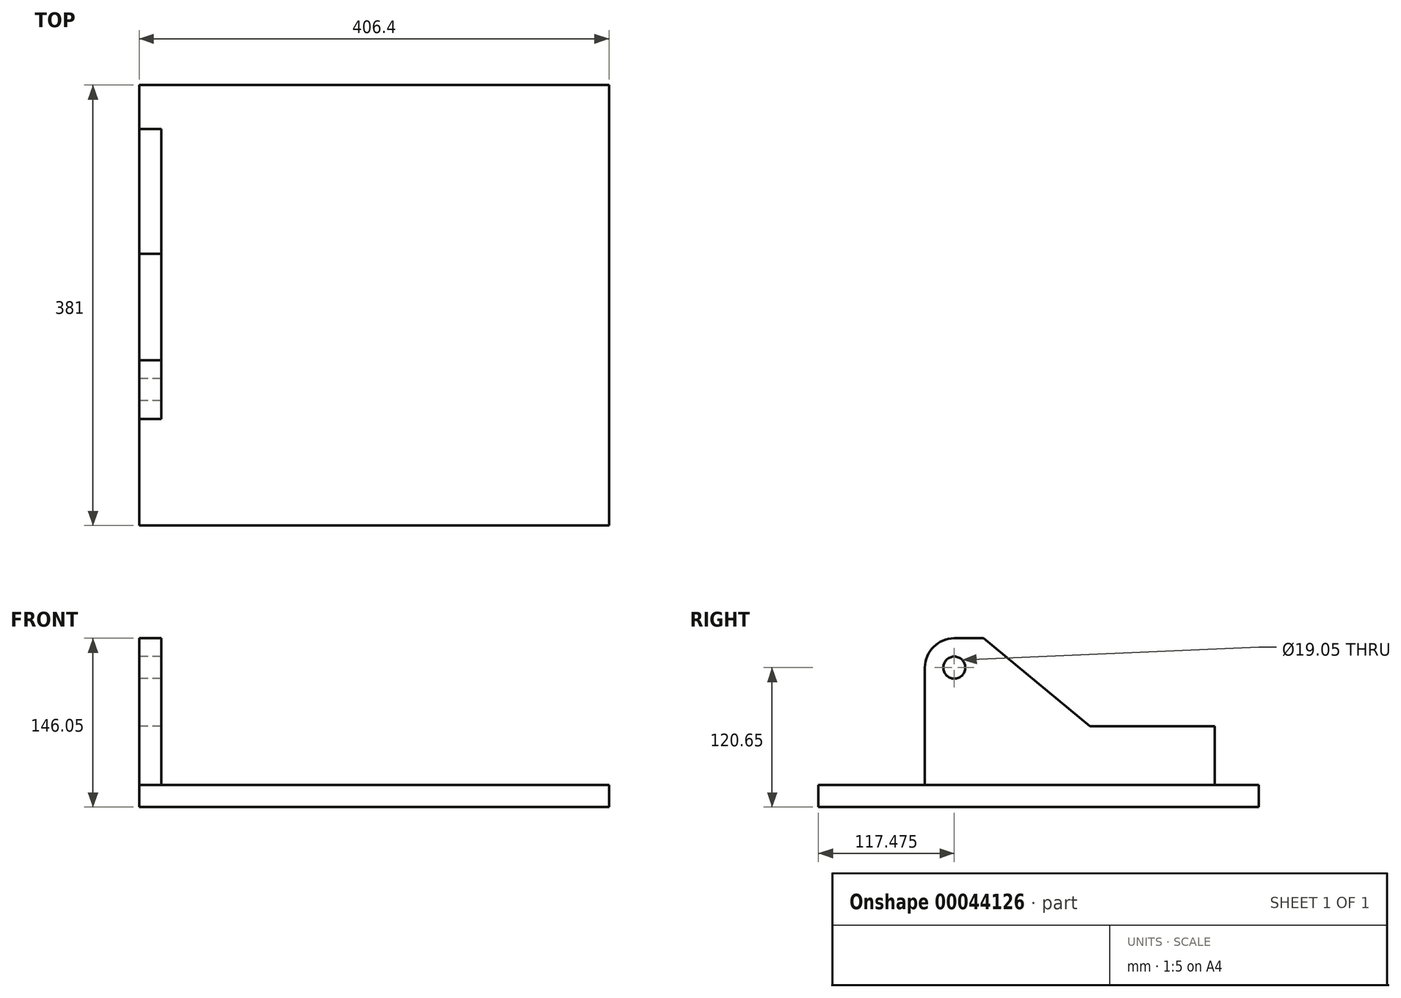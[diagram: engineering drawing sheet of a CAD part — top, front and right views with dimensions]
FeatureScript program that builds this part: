
annotation { "Feature Type Name" : "Feature", "Feature Type Description" : "" }
export const myFeature = defineFeature(function(context is Context, id is Id, definition is map)
    precondition{}
    {
        {
            var Q0;
            Q0=qCreatedBy(makeId("Right.planeOp"),FACE);
            var sketch = newSketch(context, id + "F0", { "sketchPlane" : qUnion([Q0])});
            skLineSegment(sketch, "E0.bottom", {"start": v(0, 0) * mm, "end": v(381, 0) * mm, "construction": true});
            skLineSegment(sketch, "E0.top", {"start": v(92.08, 19.05) * mm, "end": v(381, 19.05) * mm, "construction": true});
            skLineSegment(sketch, "E0.right", {"start": v(381, 0) * mm, "end": v(381, 19.05) * mm, "construction": true});
            skLineSegment(sketch, "E1.top", {"start": v(381, 107.95) * mm, "end": v(342.9, 107.95) * mm, "construction": true});
            skLineSegment(sketch, "E1.left", {"start": v(381, 19.05) * mm, "end": v(381, 107.95) * mm, "construction": true});
            skLineSegment(sketch, "E1.right", {"start": v(342.9, 19.05) * mm, "end": v(342.9, 107.95) * mm, "construction": true});
            skLineSegment(sketch, "E2.bottom", {"start": v(92.08, 19.05) * mm, "end": v(142.88, 19.05) * mm, "construction": true});
            skLineSegment(sketch, "E2.top", {"start": v(117.48, 146.05) * mm, "end": v(142.88, 146.05) * mm, "construction": true});
            skLineSegment(sketch, "E2.left", {"start": v(92.08, 19.05) * mm, "end": v(92.08, 120.65) * mm, "construction": true});
            skLineSegment(sketch, "E2.right", {"start": v(142.88, 19.05) * mm, "end": v(142.88, 146.05) * mm, "construction": true});
            skCircle(sketch, "E3", {"center": v(117.48, 120.65) * mm, "radius": 9.53 * mm, "construction": true});
            skPoint(sketch, "E3.centerSnap0", {"position": v(117.48, 146.05) * mm});
            skPoint(sketch, "E4.visualSharp", {"position": v(92.08, 146.05) * mm});
            skArc(sketch, "E4.filletArc", {"start": v(117.48, 146.05) * mm, "mid": v(99.51, 138.61) * mm, "end": v(92.08, 120.65) * mm, "construction": true});
            skLineSegment(sketch, "E5", {"start": v(142.88, 146.05) * mm, "end": v(342.9, 107.95) * mm, "construction": true});
            skLineSegment(sketch, "E6", {"start": v(0, 0) * mm, "end": v(0, 19.05) * mm, "construction": true});
            skLineSegment(sketch, "E7", {"start": v(0, 19.05) * mm, "end": v(92.08, 19.05) * mm, "construction": true});
            skSolve(sketch);
        }
        {
            var Q0;
            Q0=qCreatedBy(makeId("Right.planeOp"),FACE);
            var sketch = newSketch(context, id + "F1", { "sketchPlane" : qUnion([Q0])});
            skLineSegment(sketch, "E8.bottom", {"start": v(0, 19.05) * mm, "end": v(381, 19.05) * mm});
            skLineSegment(sketch, "E8.top", {"start": v(0, 0) * mm, "end": v(381, 0) * mm});
            skLineSegment(sketch, "E8.left", {"start": v(0, 19.05) * mm, "end": v(0, 0) * mm});
            skLineSegment(sketch, "E8.right", {"start": v(381, 19.05) * mm, "end": v(381, 0) * mm});
            skLineSegment(sketch, "E9.bottom", {"start": v(381, 19.05) * mm, "end": v(342.9, 19.05) * mm});
            skLineSegment(sketch, "E9.top", {"start": v(381, 107.95) * mm, "end": v(342.9, 107.95) * mm});
            skLineSegment(sketch, "E9.left", {"start": v(381, 19.05) * mm, "end": v(381, 107.95) * mm});
            skLineSegment(sketch, "E9.right", {"start": v(342.9, 19.05) * mm, "end": v(342.9, 107.95) * mm});
            skSolve(sketch);
        }
        {
            var Q0;
            Q0=makeQuery(id+"F1.imprint","IMPRINT",FACE,{"disambiguationData":[TD([[makeQuery(id+"F1.imprint","IMPRINT",EDGE,{"derivedFrom":sQuery(id+"F1.wireOp",EDGE,"E8.bottom")}),-1.0]])]});
            var Q1;
            Q1=makeQuery(id+"F1.imprint","IMPRINT",FACE,{"disambiguationData":[TD([[makeQuery(id+"F1.imprint","IMPRINT",EDGE,{"derivedFrom":sQuery(id+"F1.wireOp",EDGE,"E9.bottom")}),-1.0]])]});
            extrude(context, id + "F2", {"entities" : qUnion([Q0, Q1]), "depth" : 406.4 * mm});
        }
        {
            var Q0;
            Q0=qCreatedBy(makeId("Right.planeOp"),FACE);
            var sketch = newSketch(context, id + "F3", { "sketchPlane" : qUnion([Q0])});
            skLineSegment(sketch, "E10", {"start": v(92.08, 120.65) * mm, "end": v(92.08, 19.05) * mm});
            skArc(sketch, "E11", {"start": v(117.48, 146.05) * mm, "mid": v(99.51, 138.61) * mm, "end": v(92.08, 120.65) * mm});
            skCircle(sketch, "E12", {"center": v(117.48, 120.65) * mm, "radius": 9.53 * mm});
            skLineSegment(sketch, "E13", {"start": v(92.08, 19.05) * mm, "end": v(342.9, 19.05) * mm});
            skLineSegment(sketch, "E14", {"start": v(342.9, 19.05) * mm, "end": v(342.9, 107.95) * mm});
            skLineSegment(sketch, "E15", {"start": v(342.9, 69.85) * mm, "end": v(234.95, 69.85) * mm});
            skLineSegment(sketch, "E16", {"start": v(234.95, 69.85) * mm, "end": v(142.88, 146.05) * mm});
            skLineSegment(sketch, "E17", {"start": v(142.88, 146.05) * mm, "end": v(117.48, 146.05) * mm});
            skSolve(sketch);
        }
        {
            var Q0;
            Q0 = qSketchRegion(id + "F3", true);
            extrude(context, id + "F4", {"entities" : qUnion([Q0]), "depth" : 19.05 * mm});
        }
    });
